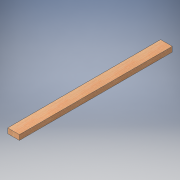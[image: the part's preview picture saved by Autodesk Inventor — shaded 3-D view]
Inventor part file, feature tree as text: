
AUTODESK INVENTOR PART (.ipt)
format: ipt  version: 2016 (Build 200138000, 138)  size: 96,768 bytes
history: native  units: in
note: dims shown in document units (in); Inventor stores cm internally (conversion verified against a paired STEP export)
features: extrude x1, sketch x1
ambient origin geometry x8: Origin, YZ Plane, XZ Plane, XY Plane, X Axis, Y Axis, Z Axis, Center Point
bodies: Solid1 (feature_tree)
feature tree (2):
  extrude  "Extrusion1"  Depth=1.5in
  sketch  "Sketch1"  dims[d0=3.5in d1=1.5in d2=45.75in d3=0.0in]
